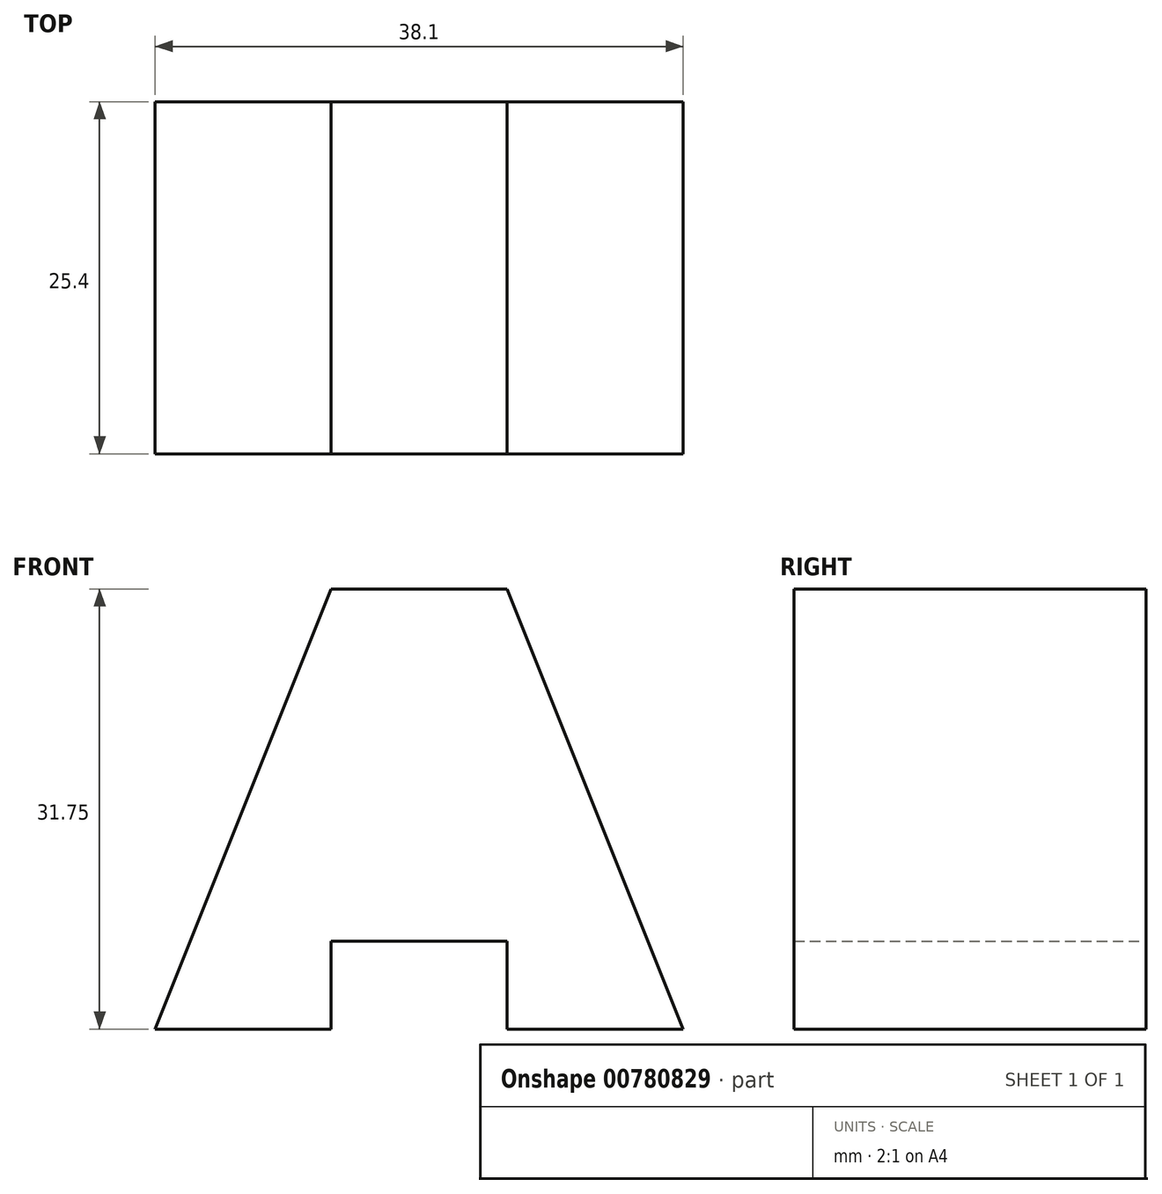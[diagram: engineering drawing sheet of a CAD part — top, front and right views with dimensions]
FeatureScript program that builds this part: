
annotation { "Feature Type Name" : "Feature", "Feature Type Description" : "" }
export const myFeature = defineFeature(function(context is Context, id is Id, definition is map)
    precondition{}
    {
        {
            var Q0;
            Q0=qCreatedBy(makeId("Front.planeOp"),FACE);
            var sketch = newSketch(context, id + "F0", { "sketchPlane" : qUnion([Q0])});
            skLineSegment(sketch, "E0", {"start": v(0, 0) * mm, "end": v(12.7, 0) * mm});
            skLineSegment(sketch, "E1", {"start": v(12.7, 0) * mm, "end": v(12.7, 6.35) * mm});
            skLineSegment(sketch, "E2", {"start": v(12.7, 6.35) * mm, "end": v(25.4, 6.35) * mm});
            skLineSegment(sketch, "E3", {"start": v(25.4, 6.35) * mm, "end": v(25.4, 0) * mm});
            skLineSegment(sketch, "E4", {"start": v(25.4, 0) * mm, "end": v(38.1, 0) * mm});
            skLineSegment(sketch, "E5", {"start": v(25.4, 31.75) * mm, "end": v(12.7, 31.75) * mm});
            skLineSegment(sketch, "E6", {"start": v(12.7, 31.75) * mm, "end": v(0, 0) * mm});
            skLineSegment(sketch, "E7", {"start": v(25.4, 23.4) * mm, "end": v(25.4, 19.05) * mm});
            skLineSegment(sketch, "E8", {"start": v(25.4, 31.75) * mm, "end": v(38.1, 0) * mm});
            skSolve(sketch);
        }
        {
            var Q0;
            Q0 = qSketchRegion(id + "F0", true);
            extrude(context, id + "F1", {"entities" : qUnion([Q0]), "depth" : 25.4 * mm, "offsetDistance" : 25.4 * mm});
        }
    });
